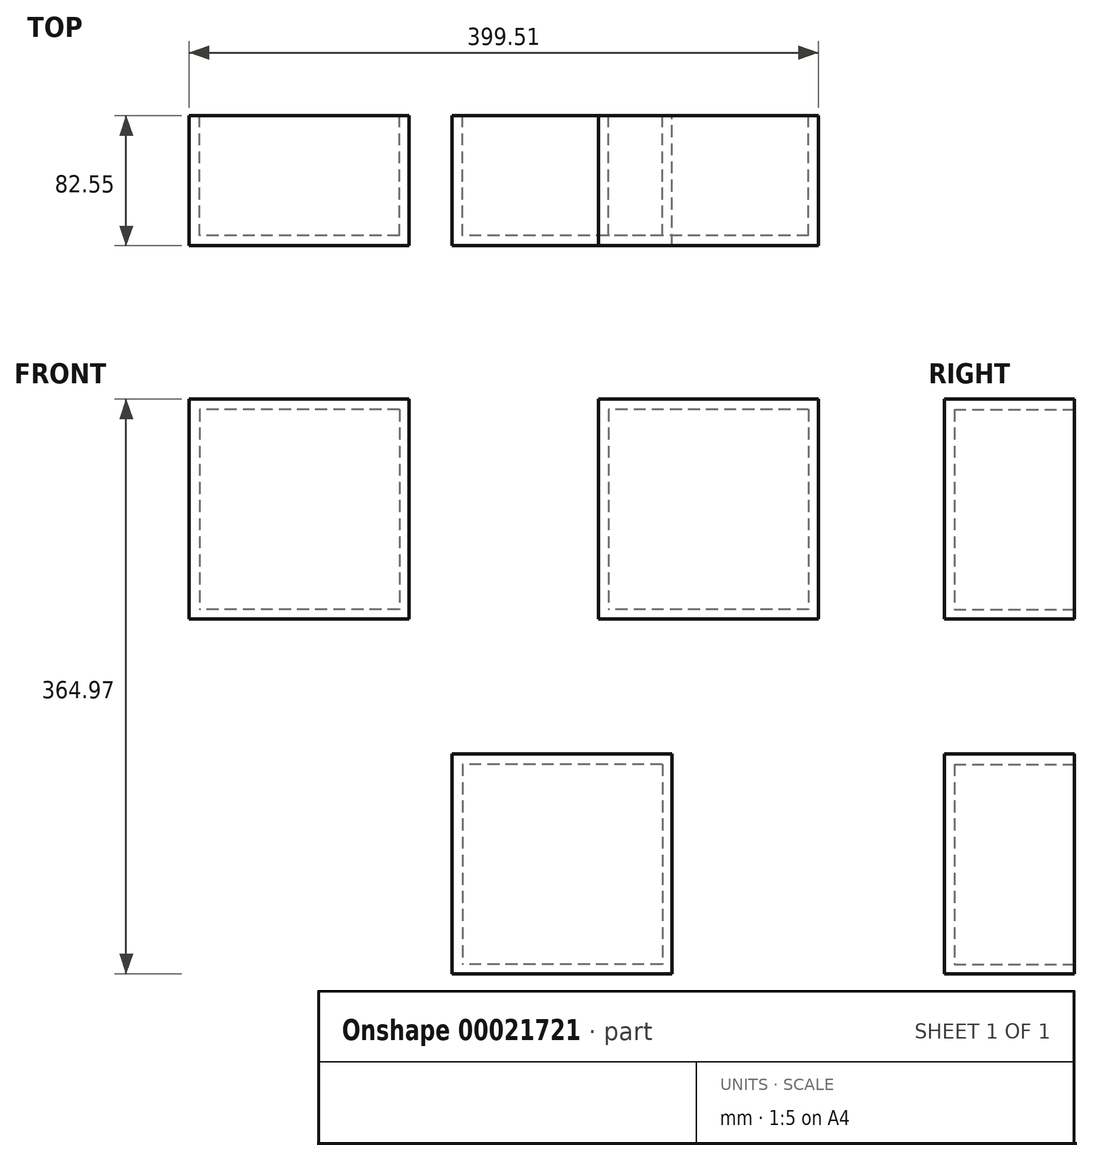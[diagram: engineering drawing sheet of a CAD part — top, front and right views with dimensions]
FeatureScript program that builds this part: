
annotation { "Feature Type Name" : "Feature", "Feature Type Description" : "" }
export const myFeature = defineFeature(function(context is Context, id is Id, definition is map)
    precondition{}
    {
        {
            var Q0;
            Q0=qCreatedBy(makeId("Front.planeOp"),FACE);
            var sketch = newSketch(context, id + "F0", { "sketchPlane" : qUnion([Q0])});
            skLineSegment(sketch, "E0.bottom", {"start": v(69.65, 140.72) * mm, "end": v(-70.05, 140.72) * mm});
            skLineSegment(sketch, "E0.left", {"start": v(69.65, 140.72) * mm, "end": v(69.65, 1.02) * mm});
            skLineSegment(sketch, "E0.right", {"start": v(-70.05, 140.72) * mm, "end": v(-70.05, 1.02) * mm});
            skLineSegment(sketch, "E1", {"start": v(-70.05, 1.02) * mm, "end": v(69.65, 1.02) * mm});
            skLineSegment(sketch, "E2.rect.bottom", {"start": v(63.5, 134.1) * mm, "end": v(-63.5, 134.1) * mm});
            skLineSegment(sketch, "E2.rect.top", {"start": v(63.5, 7.1) * mm, "end": v(-63.5, 7.1) * mm});
            skLineSegment(sketch, "E2.rect.left", {"start": v(63.5, 134.1) * mm, "end": v(63.5, 7.1) * mm});
            skLineSegment(sketch, "E2.rect.right", {"start": v(-63.5, 134.1) * mm, "end": v(-63.5, 7.1) * mm});
            skPoint(sketch, "E2.rect.middle", {"position": v(0, 70.6) * mm});
            skSolve(sketch);
        }
        {
            var Q0;
            Q0 = qSketchRegion(id + "F0", true);
            extrude(context, id + "F1", {"entities" : qUnion([Q0]), "depth" : 76.2 * mm});
        }
        {
            var Q0;
            Q0=makeQuery(id+"F1.opExtrude","CAP_FACE",FACE,{"disambiguationData":[OSD([sQuery(id+"F0.wireOp",EDGE,"E0.bottom"),sQuery(id+"F0.wireOp",EDGE,"E0.left"),sQuery(id+"F0.wireOp",EDGE,"E0.right"),sQuery(id+"F0.wireOp",EDGE,"E1"),sQuery(id+"F0.wireOp",EDGE,"E2.rect.bottom"),sQuery(id+"F0.wireOp",EDGE,"E2.rect.top"),sQuery(id+"F0.wireOp",EDGE,"E2.rect.left"),sQuery(id+"F0.wireOp",EDGE,"E2.rect.right")])],"isStart":false});
            var sketch = newSketch(context, id + "F2", { "sketchPlane" : qUnion([Q0])});
            skLineSegment(sketch, "E3.bottom", {"start": v(69.65, 1.02) * mm, "end": v(-70.05, 1.02) * mm});
            skLineSegment(sketch, "E3.top", {"start": v(69.65, 140.72) * mm, "end": v(-70.05, 140.72) * mm});
            skLineSegment(sketch, "E3.left", {"start": v(69.65, 1.02) * mm, "end": v(69.65, 140.72) * mm});
            skLineSegment(sketch, "E3.right", {"start": v(-70.05, 1.02) * mm, "end": v(-70.05, 140.72) * mm});
            skSolve(sketch);
        }
        {
            var Q0;
            Q0 = qSketchRegion(id + "F2", true);
            extrude(context, id + "F3", {"entities" : qUnion([Q0]), "operationType" : NewBodyOperationType.ADD, "depth" : 6.35 * mm});
        }
        {
            var Q0;
            Q0=makeQuery(id+"F1.opExtrude","SWEPT_BODY",BODY,{"disambiguationData":[OSD([sQuery(id+"F0.wireOp",EDGE,"E0.bottom"),sQuery(id+"F0.wireOp",EDGE,"E0.left"),sQuery(id+"F0.wireOp",EDGE,"E0.right"),sQuery(id+"F0.wireOp",EDGE,"E1"),sQuery(id+"F0.wireOp",EDGE,"E2.rect.bottom"),sQuery(id+"F0.wireOp",EDGE,"E2.rect.top"),sQuery(id+"F0.wireOp",EDGE,"E2.rect.left"),sQuery(id+"F0.wireOp",EDGE,"E2.rect.right")])]});
            var Q1;
            Q1=makeQuery(id+"F1.opExtrude","CAP_EDGE",EDGE,{"disambiguationData":[OSD([sQuery(id+"F0.wireOp",EDGE,"E0.left")])],"isStart":true});
            transform(context, id + "F4", {"entities" : qUnion([Q0]), "transformType" : TransformType.TRANSLATION_DISTANCE, "transformDirection" : qUnion([Q1]), "distance" : 25.4 * mm, "makeCopy" : true});
        }
        {
            var Q0;
            Q0=makeQuery(id+"F4.opPattern","COPY",BODY,{"derivedFrom":makeQuery(id+"F1.opExtrude","SWEPT_BODY",BODY,{"disambiguationData":[OSD([sQuery(id+"F0.wireOp",EDGE,"E0.bottom"),sQuery(id+"F0.wireOp",EDGE,"E0.left"),sQuery(id+"F0.wireOp",EDGE,"E0.right"),sQuery(id+"F0.wireOp",EDGE,"E1"),sQuery(id+"F0.wireOp",EDGE,"E2.rect.bottom"),sQuery(id+"F0.wireOp",EDGE,"E2.rect.top"),sQuery(id+"F0.wireOp",EDGE,"E2.rect.left"),sQuery(id+"F0.wireOp",EDGE,"E2.rect.right")])]}),"instanceName":"1"});
            var Q1;
            Q1=makeQuery(id+"F4.opPattern","COPY",EDGE,{"derivedFrom":makeQuery(id+"F3.opExtrude","CAP_EDGE",EDGE,{"disambiguationData":[OSD([sQuery(id+"F2.wireOp",EDGE,"E3.left")])],"isStart":false}),"instanceName":"1"});
            transform(context, id + "F5", {"entities" : qUnion([Q0]), "transformType" : TransformType.TRANSLATION_DISTANCE, "transformDirection" : qUnion([Q1]), "distance" : 199.87 * mm, "makeCopy" : false});
        }
        {
            var Q0;
            Q0=makeQuery(id+"F4.opPattern","COPY",BODY,{"derivedFrom":makeQuery(id+"F1.opExtrude","SWEPT_BODY",BODY,{"disambiguationData":[OSD([sQuery(id+"F0.wireOp",EDGE,"E0.bottom"),sQuery(id+"F0.wireOp",EDGE,"E0.left"),sQuery(id+"F0.wireOp",EDGE,"E0.right"),sQuery(id+"F0.wireOp",EDGE,"E1"),sQuery(id+"F0.wireOp",EDGE,"E2.rect.bottom"),sQuery(id+"F0.wireOp",EDGE,"E2.rect.top"),sQuery(id+"F0.wireOp",EDGE,"E2.rect.left"),sQuery(id+"F0.wireOp",EDGE,"E2.rect.right")])]}),"instanceName":"1"});
            var Q1;
            Q1=makeQuery(id+"F4.opPattern","COPY",FACE,{"derivedFrom":makeQuery(id+"F3.boolean.opBoolean","MERGE",FACE,{"derivedFrom":[makeQuery(id+"F1.opExtrude","SWEPT_FACE",FACE,{"disambiguationData":[OSD([sQuery(id+"F0.wireOp",EDGE,"E0.left")])]}),makeQuery(id+"F3.opExtrude","SWEPT_FACE",FACE,{"disambiguationData":[OSD([sQuery(id+"F2.wireOp",EDGE,"E3.left")])]})]}),"instanceName":"1"});
            var Q2;
            Q2=makeQuery(id+"F4.opPattern","COPY",FACE,{"derivedFrom":makeQuery(id+"F3.opExtrude","CAP_FACE",FACE,{"disambiguationData":[OSD([sQuery(id+"F2.wireOp",EDGE,"E3.bottom"),sQuery(id+"F2.wireOp",EDGE,"E3.top"),sQuery(id+"F2.wireOp",EDGE,"E3.left"),sQuery(id+"F2.wireOp",EDGE,"E3.right")])],"isStart":false}),"instanceName":"1"});
            transform(context, id + "F6", {"entities" : qUnion([Q0]), "transformType" : TransformType.TRANSLATION_DISTANCE, "transformDirection" : qUnion([Q1, Q2]), "distance" : 166.89 * mm, "makeCopy" : false});
        }
        {
            var Q0;
            Q0=makeQuery(id+"F1.opExtrude","SWEPT_BODY",BODY,{"disambiguationData":[OSD([sQuery(id+"F0.wireOp",EDGE,"E0.bottom"),sQuery(id+"F0.wireOp",EDGE,"E0.left"),sQuery(id+"F0.wireOp",EDGE,"E0.right"),sQuery(id+"F0.wireOp",EDGE,"E1"),sQuery(id+"F0.wireOp",EDGE,"E2.rect.bottom"),sQuery(id+"F0.wireOp",EDGE,"E2.rect.top"),sQuery(id+"F0.wireOp",EDGE,"E2.rect.left"),sQuery(id+"F0.wireOp",EDGE,"E2.rect.right")])]});
            transform(context, id + "F7", {"entities" : qUnion([Q0]), "transformType" : TransformType.TRANSLATION_3D, "dx" : 259.8 * mm, "dy" : 0 * mm, "dz" : 0 * mm, "makeCopy" : true});
        }
        {
            var Q0;
            Q0=makeQuery(id+"F1.opExtrude","SWEPT_BODY",BODY,{"disambiguationData":[OSD([sQuery(id+"F0.wireOp",EDGE,"E0.bottom"),sQuery(id+"F0.wireOp",EDGE,"E0.left"),sQuery(id+"F0.wireOp",EDGE,"E0.right"),sQuery(id+"F0.wireOp",EDGE,"E1"),sQuery(id+"F0.wireOp",EDGE,"E2.rect.bottom"),sQuery(id+"F0.wireOp",EDGE,"E2.rect.top"),sQuery(id+"F0.wireOp",EDGE,"E2.rect.left"),sQuery(id+"F0.wireOp",EDGE,"E2.rect.right")])]});
            transform(context, id + "F8", {"entities" : qUnion([Q0]), "transformType" : TransformType.TRANSLATION_3D, "dx" : 349.87 * mm, "dy" : 279 * mm, "dz" : 0 * mm, "makeCopy" : true});
        }
        {
            var Q0;
            Q0=makeQuery(id+"F8.opPattern","COPY",BODY,{"derivedFrom":makeQuery(id+"F1.opExtrude","SWEPT_BODY",BODY,{"disambiguationData":[OSD([sQuery(id+"F0.wireOp",EDGE,"E0.bottom"),sQuery(id+"F0.wireOp",EDGE,"E0.left"),sQuery(id+"F0.wireOp",EDGE,"E0.right"),sQuery(id+"F0.wireOp",EDGE,"E1"),sQuery(id+"F0.wireOp",EDGE,"E2.rect.bottom"),sQuery(id+"F0.wireOp",EDGE,"E2.rect.top"),sQuery(id+"F0.wireOp",EDGE,"E2.rect.left"),sQuery(id+"F0.wireOp",EDGE,"E2.rect.right")])]}),"instanceName":"1"});
            var Q1;
            Q1=makeQuery(id+"F8.opPattern","COPY",EDGE,{"derivedFrom":makeQuery(id+"F1.opExtrude","CAP_EDGE",EDGE,{"disambiguationData":[OSD([sQuery(id+"F0.wireOp",EDGE,"E0.bottom")])],"isStart":true}),"instanceName":"1"});
            transform(context, id + "F9", {"entities" : qUnion([Q0]), "transformType" : TransformType.TRANSLATION_DISTANCE, "transformDirection" : qUnion([Q1]), "distance" : 632.53 * mm, "makeCopy" : false});
        }
        {
            var Q0;
            Q0=makeQuery(id+"F8.opPattern","COPY",BODY,{"derivedFrom":makeQuery(id+"F1.opExtrude","SWEPT_BODY",BODY,{"disambiguationData":[OSD([sQuery(id+"F0.wireOp",EDGE,"E0.bottom"),sQuery(id+"F0.wireOp",EDGE,"E0.left"),sQuery(id+"F0.wireOp",EDGE,"E0.right"),sQuery(id+"F0.wireOp",EDGE,"E1"),sQuery(id+"F0.wireOp",EDGE,"E2.rect.bottom"),sQuery(id+"F0.wireOp",EDGE,"E2.rect.top"),sQuery(id+"F0.wireOp",EDGE,"E2.rect.left"),sQuery(id+"F0.wireOp",EDGE,"E2.rect.right")])]}),"instanceName":"1"});
            var Q1;
            Q1=makeQuery(id+"F8.opPattern","COPY",FACE,{"derivedFrom":makeQuery(id+"F3.boolean.opBoolean","MERGE",FACE,{"derivedFrom":[makeQuery(id+"F1.opExtrude","SWEPT_FACE",FACE,{"disambiguationData":[OSD([sQuery(id+"F0.wireOp",EDGE,"E0.left")])]}),makeQuery(id+"F3.opExtrude","SWEPT_FACE",FACE,{"disambiguationData":[OSD([sQuery(id+"F2.wireOp",EDGE,"E3.left")])]})]}),"instanceName":"1"});
            transform(context, id + "F10", {"entities" : qUnion([Q0]), "transformType" : TransformType.TRANSLATION_DISTANCE, "transformDirection" : qUnion([Q1]), "distance" : 97.46 * mm, "makeCopy" : false});
        }
        {
            var Q0;
            Q0=makeQuery(id+"F8.opPattern","COPY",BODY,{"derivedFrom":makeQuery(id+"F1.opExtrude","SWEPT_BODY",BODY,{"disambiguationData":[OSD([sQuery(id+"F0.wireOp",EDGE,"E0.bottom"),sQuery(id+"F0.wireOp",EDGE,"E0.left"),sQuery(id+"F0.wireOp",EDGE,"E0.right"),sQuery(id+"F0.wireOp",EDGE,"E1"),sQuery(id+"F0.wireOp",EDGE,"E2.rect.bottom"),sQuery(id+"F0.wireOp",EDGE,"E2.rect.top"),sQuery(id+"F0.wireOp",EDGE,"E2.rect.left"),sQuery(id+"F0.wireOp",EDGE,"E2.rect.right")])]}),"instanceName":"1"});
            deleteBodies(context, id + "F11", {"entities" : qUnion([Q0])});
        }
    });
